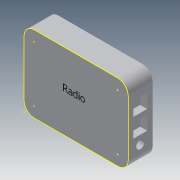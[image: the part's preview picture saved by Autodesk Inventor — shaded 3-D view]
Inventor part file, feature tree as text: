
AUTODESK INVENTOR PART (.ipt)
format: ipt  version: 2014 (Build 180170000, 170)  size: 125,440 bytes
history: native  units: in
note: dims shown in document units (in); Inventor stores cm internally (conversion verified against a paired STEP export)
features: sketch x4, extrude x3
ambient origin geometry x8: Origin, YZ Plane, XZ Plane, XY Plane, X Axis, Y Axis, Z Axis, Center Point
bodies: Solid1 (feature_tree)
feature tree (7):
  extrude  "Extrusion1"  Depth=2.75in
  extrude  "Extrusion2"  Depth=0.875in TaperAngle=0.0deg
  extrude  "Extrusion3"  Depth=0.375in
  sketch  "Sketch4"  dims[d8=0.375in d9=0.375in d10=0.375in d11=0.125in d12=0.0in]
  sketch  "Sketch1"  dims[d0=3.75in d1=2.75in]
  sketch  "Sketch2"  dims[d2=0.375in d3=0.875in d4=0.0in]
  sketch  "Sketch3"  dims[d5=0.25in d6=0.0in d7=0.375in]
